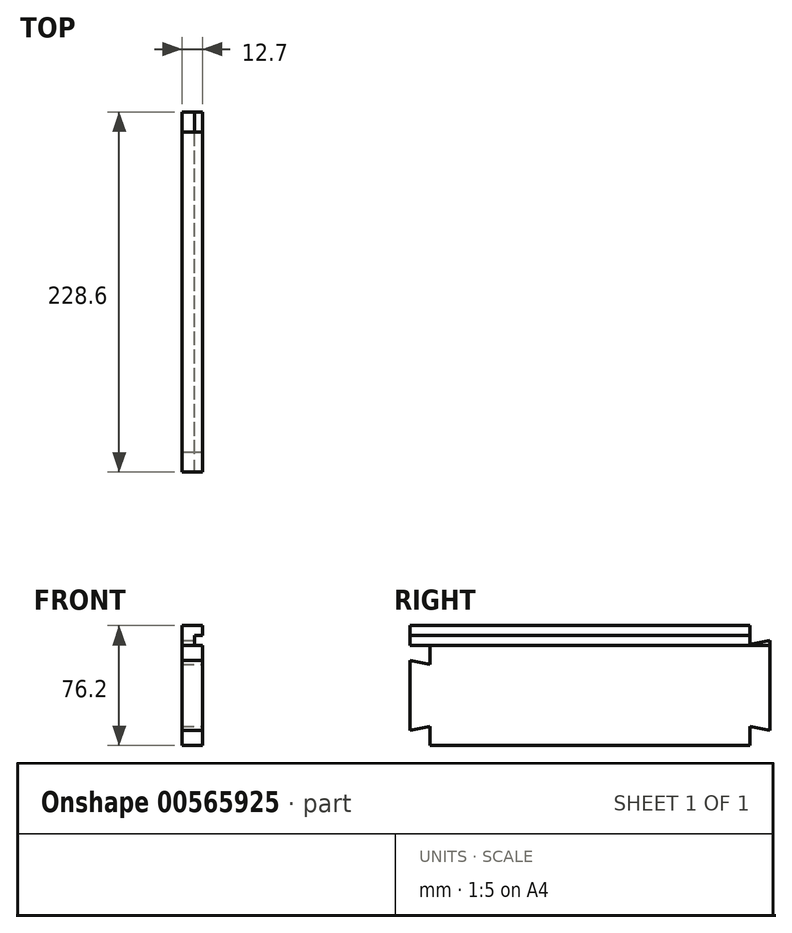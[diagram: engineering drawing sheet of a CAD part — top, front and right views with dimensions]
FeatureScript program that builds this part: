
annotation { "Feature Type Name" : "Feature", "Feature Type Description" : "" }
export const myFeature = defineFeature(function(context is Context, id is Id, definition is map)
    precondition{}
    {
        {
            var Q0;
            Q0=qCreatedBy(makeId("Front.planeOp"),FACE);
            var sketch = newSketch(context, id + "F0", { "sketchPlane" : qUnion([Q0])});
            skLineSegment(sketch, "E0.bottom", {"start": v(-6.35, 38.1) * mm, "end": v(6.35, 38.1) * mm});
            skLineSegment(sketch, "E0.top", {"start": v(-6.35, -38.1) * mm, "end": v(6.35, -38.1) * mm});
            skLineSegment(sketch, "E0.left", {"start": v(-6.35, 38.1) * mm, "end": v(-6.35, -38.1) * mm});
            skLineSegment(sketch, "E0.right", {"start": v(6.35, 38.1) * mm, "end": v(6.35, -38.1) * mm});
            skLineSegment(sketch, "E1", {"start": v(-6.35, 38.1) * mm, "end": v(6.35, -38.1) * mm, "construction": true});
            skSolve(sketch);
        }
        {
            var Q0;
            Q0 = qSketchRegion(id + "F0", true);
            extrude(context, id + "F1", {"entities" : qUnion([Q0]), "endBound" : BoundingType.SYMMETRIC, "depth" : 228.6 * mm, "offsetDistance" : 25.4 * mm});
        }
        {
            var Q0;
            {var subQ0=sQuery(id+"F0.wireOp",EDGE,"E0.right");var subQ2=sQuery(id+"F0.wireOp",EDGE,"E0.top");var subQ5=makeQuery(id+"F5.opExtrude","SWEPT_FACE",FACE,{"disambiguationData":[OSD([sQuery(id+"F4.wireOp",EDGE,"E23.0")])]});Q0=makeQuery(id+"FtgXUjz83fswi7n_1.boolean.opBoolean","SPLIT",FACE,{"disambiguationData":[TD([makeQuery(id+"F5.boolean.opBoolean","COPY",FACE,{"derivedFrom":subQ5})])],"derivedFrom":makeQuery(id+"F5.boolean.opBoolean","SPLIT",FACE,{"disambiguationData":[TD([makeQuery(id+"F1.opExtrude","SWEPT_FACE",FACE,{"disambiguationData":[OSD([subQ2])]})])],"derivedFrom":makeQuery(id+"F1.opExtrude","SWEPT_FACE",FACE,{"disambiguationData":[OSD([subQ0])]})})});}
            var sketch = newSketch(context, id + "F2", { "sketchPlane" : qUnion([Q0])});
            skLineSegment(sketch, "E2", {"start": v(-114.3, 25.4) * mm, "end": v(-101.6, 25.4) * mm});
            skLineSegment(sketch, "E3", {"start": v(-114.3, 25.4) * mm, "end": v(-114.3, 15.87) * mm});
            skLineSegment(sketch, "E4", {"start": v(-114.3, 15.87) * mm, "end": v(-101.6, 13.34) * mm});
            skLineSegment(sketch, "E5", {"start": v(-101.6, 13.34) * mm, "end": v(-101.6, 25.4) * mm});
            skLineSegment(sketch, "E6", {"start": v(-114.3, 15.87) * mm, "end": v(-81.41, 15.88) * mm, "construction": true});
            skLineSegment(sketch, "E7", {"start": v(-114.3, 25.4) * mm, "end": v(-114.3, -38.1) * mm, "construction": true});
            skLineSegment(sketch, "E8", {"start": v(-114.3, -6.35) * mm, "end": v(-42.34, -6.35) * mm, "construction": true});
            skLineSegment(sketch, "E9.MirrorCS", {"start": v(-114.3, -38.1) * mm, "end": v(-101.6, -38.1) * mm});
            skLineSegment(sketch, "E10.MirrorCS", {"start": v(-101.6, -26.04) * mm, "end": v(-101.6, -38.1) * mm});
            skLineSegment(sketch, "E11.MirrorCS", {"start": v(-114.3, -28.57) * mm, "end": v(-101.6, -26.04) * mm});
            skLineSegment(sketch, "E12.MirrorCS", {"start": v(-114.3, -38.1) * mm, "end": v(-114.3, -28.57) * mm});
            skLineSegment(sketch, "E13", {"start": v(114.3, 38.1) * mm, "end": v(101.6, 38.1) * mm});
            skLineSegment(sketch, "E14", {"start": v(114.3, 38.1) * mm, "end": v(114.3, 28.57) * mm});
            skLineSegment(sketch, "E15", {"start": v(101.6, 38.1) * mm, "end": v(101.6, 26.04) * mm});
            skLineSegment(sketch, "E16", {"start": v(101.6, 26.04) * mm, "end": v(114.3, 28.57) * mm});
            skLineSegment(sketch, "E17.MirrorCS", {"start": v(114.3, -38.1) * mm, "end": v(114.3, -28.57) * mm});
            skLineSegment(sketch, "E18.MirrorCS", {"start": v(101.6, -38.1) * mm, "end": v(101.6, -26.04) * mm});
            skLineSegment(sketch, "E19.MirrorCS", {"start": v(101.6, -26.04) * mm, "end": v(114.3, -28.57) * mm});
            skLineSegment(sketch, "E20.MirrorCS", {"start": v(114.3, -38.1) * mm, "end": v(101.6, -38.1) * mm});
            skLineSegment(sketch, "E21", {"start": v(114.3, 28.57) * mm, "end": v(83.32, 28.57) * mm, "construction": true});
            skSolve(sketch);
        }
        {
            var Q0;
            Q0 = qSketchRegion(id + "F2", true);
            var Q1;
            Q1=makeQuery(id+"F1.opExtrude","SWEPT_FACE",FACE,{"disambiguationData":[OSD([sQuery(id+"F0.wireOp",EDGE,"E0.left")])]});
            extrude(context, id + "F3", {"entities" : qUnion([Q0]), "operationType" : NewBodyOperationType.REMOVE, "endBound" : BoundingType.UP_TO_SURFACE, "oppositeDirection" : true, "depth" : 25.4 * mm, "endBoundEntityFace" : qUnion([Q1]), "offsetDistance" : 25.4 * mm});
        }
        {
            var Q0;
            Q0=makeQuery(id+"F1.opExtrude","SWEPT_FACE",FACE,{"disambiguationData":[OSD([sQuery(id+"F0.wireOp",EDGE,"E0.right")])]});
            var sketch = newSketch(context, id + "F4", { "sketchPlane" : qUnion([Q0])});
            skLineSegment(sketch, "E22.0", {"start": v(-114.3, 31.75) * mm, "end": v(114.3, 31.75) * mm});
            skLineSegment(sketch, "E23.0", {"start": v(-114.3, 25.4) * mm, "end": v(114.3, 25.4) * mm});
            skLineSegment(sketch, "E24", {"start": v(-114.3, 31.75) * mm, "end": v(-114.3, 25.4) * mm});
            skLineSegment(sketch, "E25", {"start": v(114.3, 31.75) * mm, "end": v(114.3, 25.4) * mm});
            skSolve(sketch);
        }
        {
            var Q0;
            Q0 = qSketchRegion(id + "F4", true);
            extrude(context, id + "F5", {"entities" : qUnion([Q0]), "operationType" : NewBodyOperationType.REMOVE, "oppositeDirection" : true, "depth" : 4.76 * mm, "offsetDistance" : 25.4 * mm});
        }
    });
